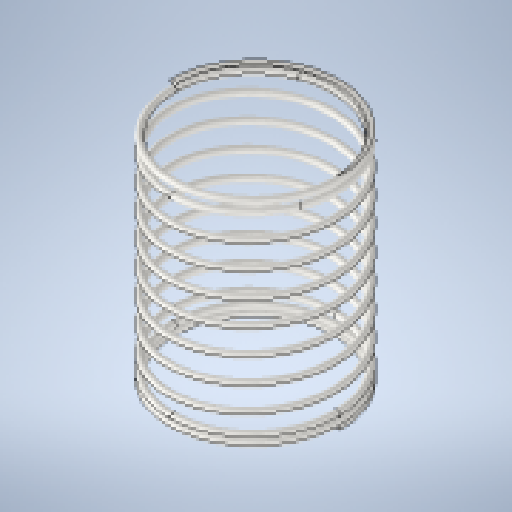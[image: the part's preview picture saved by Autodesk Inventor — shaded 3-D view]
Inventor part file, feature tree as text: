
AUTODESK INVENTOR PART (.ipt)
format: ipt  version: 2025 (Build 290162010, 162A)  size: 987,136 bytes
history: native  units: mm
features: other x67, extrude x8, helix x5, sketch x3, sweep x2, plane x1
ambient origin geometry x8: Origin, YZ Plane, XZ Plane, XY Plane, X Axis, Y Axis, Z Axis, Center Point
bodies: Solid1 (feature_tree)
feature tree (86):
  other  "Main Coil Path(Right)"
  other  "Section Work Plane(Right)"
  other  "Start Work Plane(Right)"
  other  "End Work Plane(Right)"
  other  "End Cut Work Plane(Right)"
  other  "Start Cut Work Plane(Right)"
  other  "Plain Ends Cut Work Plane 1(Right)"
  other  "Plain Ends Cut Work Plane 2(Right)"
  sweep  "Main Coil Feature(R)"
  other  "Start Transition Coil 1(Right)"
  helix  "Coil  Start Transition 2(R)"  [1 undecoded]
  helix  "Coil  Start Transition 3(R)"  [1 undecoded]
  helix  "Coil  Start Transition 4(R)"  [1 undecoded]
  other  "Start Ends Coil(Right)"
  extrude  "Start Cut Feature(Right)"  Depth=10.0mm
  other  "End Transition Coil 1(Right)"
  other  "End Transition Coil 2(Right)"
  other  "End Transition Coil 3(Right)"
  other  "End Transition Coil 4(Right)"
  other  "End Coil(Right)"
  extrude  "End Cut Feature(Right)"  Depth=10.0mm
  extrude  "Plain Ends Cut Feature 1(Right)"  Depth=10.0mm
  extrude  "Plain Ends Cut  2(R)"  Depth=10.0mm TaperAngle=0.0deg
  other  "Main Coil Path(Left)"
  other  "Section Work Plane(Left)"
  other  "Start Work Plane(Left)"
  other  "End Work Plane(Left)"
  other  "End Cut Work Plane(Left)"
  other  "Start Cut Work Plane(Left)"
  other  "Plain Ends Cut Work Plane 1(Left)"
  other  "Plain Ends Cut Work Plane 2(Left)"
  sweep  "Main Coil Feature(L)"
  other  "Start Transition Coil 1(Left)"
  other  "Start Transition Coil 2(Left)"
  other  "Start Transition Coil 3(Left)"
  other  "Start Transition Coil 4(Left)"
  other  "Start Ends Coil(Left)"
  extrude  "Start Cut Feature(Left)"  Depth=10.0mm TaperAngle=0.0deg
  other  "End Transition Coil 1(Left)"
  other  "End Transition Coil 2(Left)"
  other  "End Transition Coil 3(Left)"
  other  "End Transition Coil 4(Left)"
  other  "End Coil(Left)"
  extrude  "End Cut Feature(Left)"  Depth=10.0mm
  extrude  "Cut Plain Ends Cut 1(L)"  TaperAngle=0.0deg  [1 undecoded]
  extrude  "Cut Plain Ends Cut 2(L)"  TaperAngle=0.0deg  [1 undecoded]
  other  "iMate Based Work Plane"
  other  "Preview Center Point"
  other  "Preview X Axis"
  other  "Path Section Sketch(Right)"
  other  "Srf1"
  helix  "Coil Section Sketch(Right)"  [1 undecoded]
  other  "Start Transition Coil Sketch 1(Right)"
  sketch  "Sketch  Start Transition 2(R)"  dims[d0=0.125mm d2=1.062272mm d3=10.0mm d4=81.25mm]
  sketch  "Sketch  Start Transition 3(R)"  dims[d5=0.0mm d6=90.0deg d7=90.0deg d8=0.0mm d9=0.0mm d12=1.033139mm d13=-1.335902mm d14=0.5mm]
  sketch  "Sketch  Start Transition 4(R)"  dims[d15=0.0mm d16=0.921704mm d17=10.0mm d18=2.5mm d19=0.0mm d20=90.0deg d21=90.0deg d22=0.0mm d23=0.0mm d24=0.781136mm d25=10.0mm d26=2.5mm d27=0.0mm d28=90.0deg d29=90.0deg d30=0.0mm d31=0.0mm d32=0.640568mm d33=10.0mm d34=2.5mm d35=0.0mm d36=90.0deg d37=90.0deg d38=0.0mm d39=0.0mm d40=0.5mm d41=10.0mm d42=2.5mm d43=0.0mm d44=90.0deg d45=90.0deg d46=0.0mm d47=0.0mm d48=0.921704mm d49=10.0mm d50=1.875mm d51=0.0mm d52=90.0deg d53=90.0deg d54=0.0mm d55=0.0mm d56=0.781136mm d57=10.0mm d58=1.875mm d59=0.0mm d60=90.0deg d61=90.0deg d62=0.0mm d63=0.0mm d64=0.640568mm d65=10.0mm d66=1.875mm d67=0.0mm d68=90.0deg d69=90.0deg d70=0.0mm d71=0.0mm d72=0.5mm d73=10.0mm d74=1.875mm d75=0.0mm d76=90.0deg d77=90.0deg d78=0.0mm d79=0.0mm d81=10.0mm d82=15.0mm d83=0.0mm d84=90.0deg d85=90.0deg d86=0.0mm d87=0.0mm d88=0.500198mm d89=10.0mm d90=10.0mm d91=0.0mm d92=90.0deg d93=90.0deg d94=0.0mm d95=0.0mm d96=12.5mm d97=0.500198mm d98=0.0mm d99=12.5mm d100=0.500198mm d101=0.0mm d102=0.0mm d103=0.0mm d104=0.0mm d105=0.0mm d106=0.0mm d108=0.0mm d112=0.0mm d113=0.0mm d114=0.0mm d121=0.125248mm d131=0.0mm d132=0.0mm d133=0.0mm d134=0.0mm d135=0.125mm d137=1.062272mm d138=10.0mm d139=81.25mm d140=0.0mm d141=90.0deg d142=90.0deg d143=0.0mm d144=0.0mm d145=1.033139mm d146=-1.335902mm d147=0.125248mm d148=0.000198mm d149=0.5mm d150=0.0mm d151=0.0mm d152=0.921704mm d153=10.0mm d154=2.5mm d155=0.0mm d156=90.0deg d157=90.0deg d158=0.0mm d159=0.0mm d160=0.781136mm d161=10.0mm d162=2.5mm d163=0.0mm d164=90.0deg d165=90.0deg d166=0.0mm d167=0.0mm d168=0.640568mm d169=10.0mm d170=2.5mm d171=0.0mm d172=90.0deg d173=90.0deg d174=0.0mm d175=0.0mm d176=0.5mm d177=10.0mm d178=2.5mm d179=0.0mm d180=90.0deg d181=90.0deg d182=0.0mm d183=0.0mm d184=10.0mm d185=10.0mm d186=10.0mm d187=10.0mm d188=0.500198mm d189=10.0mm d190=15.0mm d191=0.0mm d192=90.0deg d193=90.0deg d194=0.0mm d195=0.0mm d196=10.0mm d197=12.5mm d198=0.500198mm d199=0.0mm d200=10.0mm d201=0.921704mm d202=10.0mm d203=1.875mm d204=0.0mm d205=90.0deg d206=90.0deg d207=0.0mm d208=0.0mm d209=10.0mm d210=0.781136mm d211=10.0mm d212=1.875mm d213=0.0mm d214=90.0deg d215=90.0deg d216=0.0mm d217=0.0mm d218=0.640568mm d219=10.0mm d220=1.875mm d221=0.0mm d222=90.0deg d223=90.0deg d224=0.0mm d225=0.0mm d226=0.5mm d227=10.0mm d228=1.875mm d229=0.0mm d230=90.0deg d231=90.0deg d232=0.0mm d233=0.0mm d234=10.0mm d235=10.0mm d236=10.0mm d237=0.500198mm d238=10.0mm d239=10.0mm d240=0.0mm d241=90.0deg d242=90.0deg d243=0.0mm d244=0.0mm d245=12.5mm d246=0.500198mm d247=0.0mm d248=10.0mm d249=10.0mm d254=12.5mm d255=10.0mm d256=0.0mm d257=20.0mm d258=-0.000198mm d259=12.5mm d260=10.0mm d261=0.0mm d262=10.0mm d263=12.5mm d264=10.0mm d265=0.0mm d266=10.0mm d267=0.0mm d270=-1.273402mm d271=0.0mm d272=12.5mm d273=10.0mm d274=0.0mm d275=20.0mm d276=-157.079633mm d277=12.0mm d278=12.0mm d279=0.0mm d280=0.0mm]
  other  "End Transition Coil Sketch 1(Right)"
  other  "End Transition Coil Sketch 2(Right)"
  other  "End Transition Coil Sketch 3(Right)"
  other  "End Transition Coil Sketch 4(Right)"
  other  "Start Ends Skecth(Right)"
  other  "End Coil Skecth(Right)"
  other  "End Cut Sketch(Right)"
  other  "Start Cut Sketch(Right)"
  other  "Path Section Sketch(Left)"
  other  "Srf2"
  helix  "Coil Section Sketch(Left)"  [1 undecoded]
  other  "Start Transition Coil Sketch 1(Left)"
  other  "Start Transition Coil Sketch 2(Left)"
  other  "Start Transition Coil Sketch 3(Left)"
  other  "Start Transition Coil Sketch 4(Left)"
  other  "Start Ends Skecth(Left)"
  other  "Start Cut Sketch(Left)"
  other  "End Transition Coil Sketch 1(Left)"
  other  "End Transition Coil Sketch 2(Left)"
  other  "End Transition Coil Sketch 3(Left)"
  other  "End Transition Coil Sketch 4(Left)"
  other  "End Coil Skecth(Left)"
  other  "End Cut Sketch(Left)"
  other  "Plain Ends Cut Sketch 2(Left)"
  other  "Plain Ends Cut Sketch 2(Right)"
  other  "Plain Ends Cut Sketch 1(Right)"
  other  "Plain Ends Cut Sketch 1(Left)"
  plane  "Work Plane Start Section"
  other  "Basic Curve(Right)"
  other  "Basic Curve(Left)"
note: 7 required parameter values undecoded (feature->parameter linkage not recoverable at this tier; creation-order binding heuristic only, values carry confidence <= 0.55)
